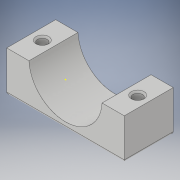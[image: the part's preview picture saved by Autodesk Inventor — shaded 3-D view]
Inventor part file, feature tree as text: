
AUTODESK INVENTOR PART (.ipt)
format: ipt  version: 2019 (Build 230136000, 136)  size: 173,056 bytes
history: native  units: mm
features: sketch x6, extrude x3, hole x2, fillet x1
ambient origin geometry x8: Origin, YZ Plane, XZ Plane, XY Plane, X Axis, Y Axis, Z Axis, Center Point
bodies: Solid1 (feature_tree)
feature tree (12):
  extrude  "Extrusion1"  Depth=60.0mm
  extrude  "Extrusion2"  Depth=25.0mm TaperAngle=0.0deg
  sketch  "Sketch3"  dims[d5=1.0mm d6=10.0mm d7=0.0mm]
  hole  "Hole1"  [1 undecoded]
  extrude  "Extrusion3"  Depth=3.0mm
  hole  "Hole3"  [1 undecoded]
  fillet  "Fillet1"  Radius=12.0mm
  sketch  "Sketch1"  dims[d0=37.35mm d1=60.0mm]
  sketch  "Sketch2"  dims[d2=55.0mm d3=25.0mm d4=0.0mm]
  sketch  "Sketch4"  dims[d8=4.9mm d9=6.0mm d10=6.5mm d11=7.0mm d12=14.835299mm d13=6.0mm d14=90.0deg d23=3.0mm]
  sketch  "Sketch6"  dims[d24=10.0mm d25=0.0mm d26=40.0mm d27=12.0mm]
  sketch  "Sketch7"  dims[d28=4.9mm d29=6.0mm d30=6.5mm d31=7.0mm d32=14.835299mm d33=6.0mm d34=90.0deg d35=1.2mm]
note: 2 required parameter values undecoded (feature->parameter linkage not recoverable at this tier; creation-order binding heuristic only, values carry confidence <= 0.55)
